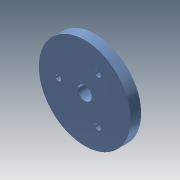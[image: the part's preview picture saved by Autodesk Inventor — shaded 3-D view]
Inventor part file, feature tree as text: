
AUTODESK INVENTOR PART (.ipt)
format: ipt  version: 2013 (Build 170138000, 138)  size: 108,032 bytes
history: native  units: mm
features: sketch x4, extrude x3
ambient origin geometry x8: Origin, YZ Plane, XZ Plane, XY Plane, X Axis, Y Axis, Z Axis, Center Point
bodies: Solid1 (feature_tree)
feature tree (7):
  extrude  "Extrusion1"  Depth=5.0mm
  extrude  "Extrusion2"  Depth=3.0mm
  extrude  "Extrusion3"  Depth=3.0mm
  sketch  "Sketch4"  dims[d9=3.8mm d10=0.0mm d11=2.0mm d12=2.0mm d13=2.0mm d14=3.8mm d15=0.0mm]
  sketch  "Sketch1"  dims[d0=33.15mm d1=5.0mm]
  sketch  "Sketch2"  dims[d2=3.8mm d3=0.0mm d4=3.0mm]
  sketch  "Sketch3"  dims[d7=3.0mm d8=3.0mm]
